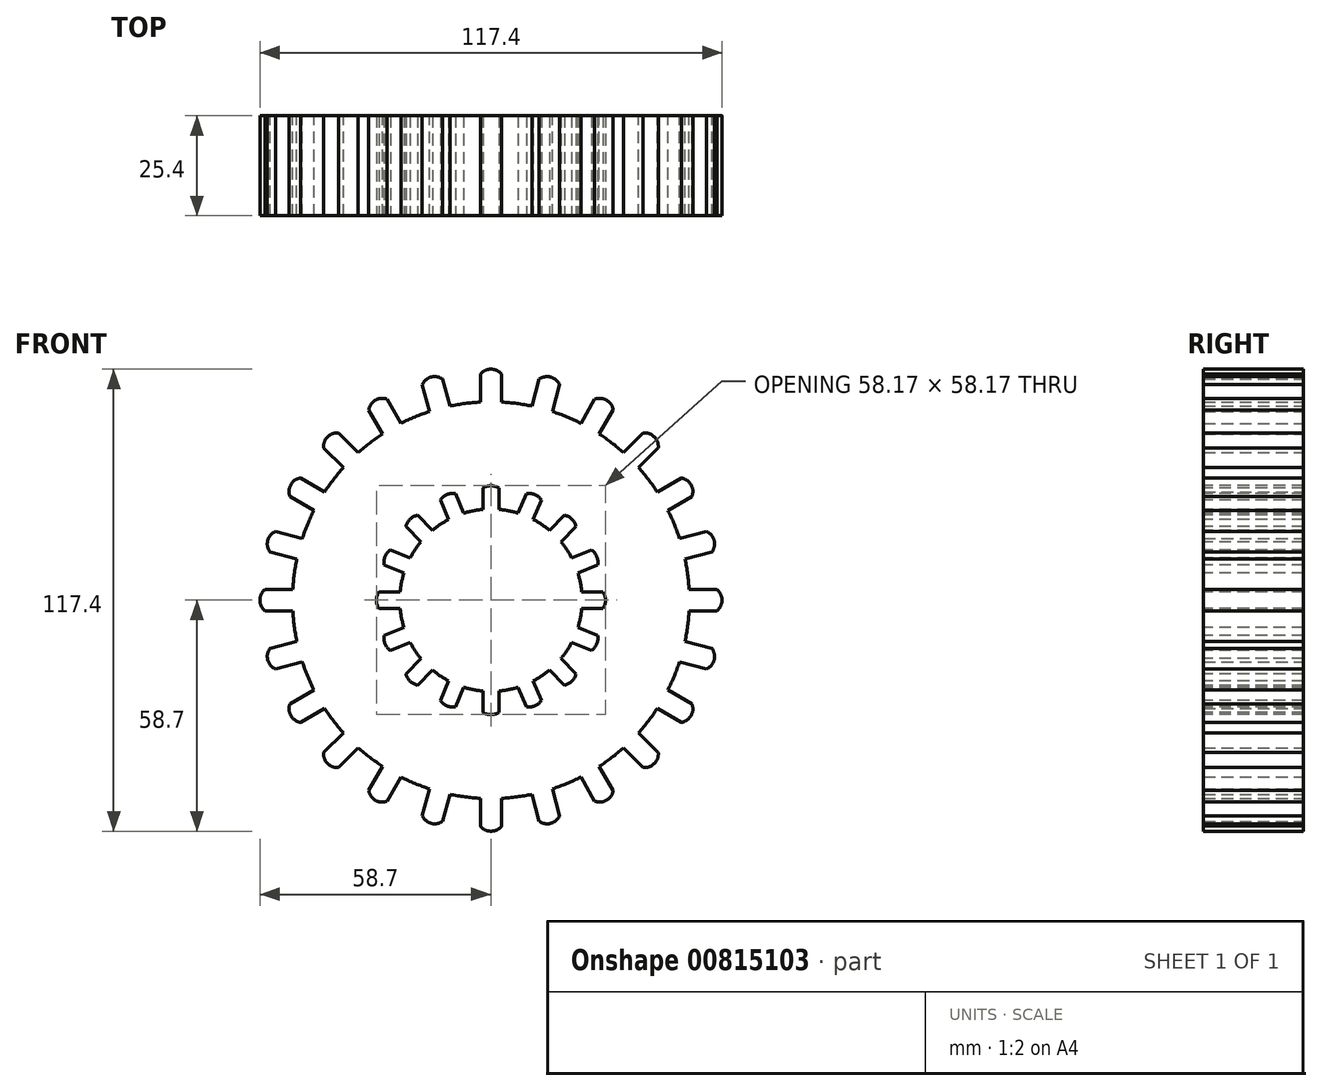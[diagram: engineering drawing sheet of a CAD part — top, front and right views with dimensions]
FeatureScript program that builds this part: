
annotation { "Feature Type Name" : "Feature", "Feature Type Description" : "" }
export const myFeature = defineFeature(function(context is Context, id is Id, definition is map)
    precondition{}
    {
        {
            var Q0;
            Q0=qCreatedBy(makeId("Front.planeOp"),FACE);
            var sketch = newSketch(context, id + "F0", { "sketchPlane" : qUnion([Q0])});
            skCircle(sketch, "E0", {"center": v(0, 0) * mm, "radius": 50.41 * mm});
            skLineSegment(sketch, "E1", {"start": v(2.7, 57.4) * mm, "end": v(2.7, 50.34) * mm});
            skLineSegment(sketch, "E2.MirrorCS", {"start": v(-2.7, 57.4) * mm, "end": v(-2.7, 50.34) * mm});
            skArc(sketch, "E3", {"start": v(2.7, 57.4) * mm, "mid": v(0, 58.7) * mm, "end": v(-2.7, 57.4) * mm});
            skLineSegment(sketch, "E4.1.0", {"start": v(-17.46, 54.75) * mm, "end": v(-15.63, 47.93) * mm});
            skArc(sketch, "E4.1.1", {"start": v(-12.25, 56.15) * mm, "mid": v(-15.2, 56.7) * mm, "end": v(-17.46, 54.75) * mm});
            skLineSegment(sketch, "E4.1.2", {"start": v(-12.25, 56.15) * mm, "end": v(-10.43, 49.32) * mm});
            skLineSegment(sketch, "E4.2.0", {"start": v(-31.04, 48.37) * mm, "end": v(-27.5, 42.25) * mm});
            skArc(sketch, "E4.2.1", {"start": v(-26.37, 51.06) * mm, "mid": v(-29.35, 50.84) * mm, "end": v(-31.04, 48.37) * mm});
            skLineSegment(sketch, "E4.2.2", {"start": v(-26.37, 51.06) * mm, "end": v(-22.84, 44.94) * mm});
            skLineSegment(sketch, "E4.3.0", {"start": v(-42.5, 38.69) * mm, "end": v(-37.5, 33.7) * mm});
            skArc(sketch, "E4.3.1", {"start": v(-38.69, 42.5) * mm, "mid": v(-41.5, 41.5) * mm, "end": v(-42.5, 38.69) * mm});
            skLineSegment(sketch, "E4.3.2", {"start": v(-38.69, 42.5) * mm, "end": v(-33.7, 37.5) * mm});
            skLineSegment(sketch, "E4.4.0", {"start": v(-51.06, 26.37) * mm, "end": v(-44.94, 22.84) * mm});
            skArc(sketch, "E4.4.1", {"start": v(-48.37, 31.04) * mm, "mid": v(-50.84, 29.35) * mm, "end": v(-51.06, 26.37) * mm});
            skLineSegment(sketch, "E4.4.2", {"start": v(-48.37, 31.04) * mm, "end": v(-42.25, 27.5) * mm});
            skLineSegment(sketch, "E4.5.0", {"start": v(-56.15, 12.25) * mm, "end": v(-49.32, 10.43) * mm});
            skArc(sketch, "E4.5.1", {"start": v(-54.75, 17.46) * mm, "mid": v(-56.7, 15.2) * mm, "end": v(-56.15, 12.25) * mm});
            skLineSegment(sketch, "E4.5.2", {"start": v(-54.75, 17.46) * mm, "end": v(-47.93, 15.63) * mm});
            skLineSegment(sketch, "E4.6.0", {"start": v(-57.4, -2.7) * mm, "end": v(-50.34, -2.7) * mm});
            skArc(sketch, "E4.6.1", {"start": v(-57.4, 2.7) * mm, "mid": v(-58.7, 0) * mm, "end": v(-57.4, -2.7) * mm});
            skLineSegment(sketch, "E4.6.2", {"start": v(-57.4, 2.7) * mm, "end": v(-50.34, 2.7) * mm});
            skLineSegment(sketch, "E4.7.0", {"start": v(-54.75, -17.46) * mm, "end": v(-47.93, -15.63) * mm});
            skArc(sketch, "E4.7.1", {"start": v(-56.15, -12.25) * mm, "mid": v(-56.7, -15.2) * mm, "end": v(-54.75, -17.46) * mm});
            skLineSegment(sketch, "E4.7.2", {"start": v(-56.15, -12.25) * mm, "end": v(-49.32, -10.43) * mm});
            skLineSegment(sketch, "E4.8.0", {"start": v(-48.37, -31.04) * mm, "end": v(-42.25, -27.5) * mm});
            skArc(sketch, "E4.8.1", {"start": v(-51.06, -26.37) * mm, "mid": v(-50.84, -29.35) * mm, "end": v(-48.37, -31.04) * mm});
            skLineSegment(sketch, "E4.8.2", {"start": v(-51.06, -26.37) * mm, "end": v(-44.94, -22.84) * mm});
            skLineSegment(sketch, "E4.9.0", {"start": v(-38.69, -42.5) * mm, "end": v(-33.7, -37.5) * mm});
            skArc(sketch, "E4.9.1", {"start": v(-42.5, -38.69) * mm, "mid": v(-41.5, -41.5) * mm, "end": v(-38.69, -42.5) * mm});
            skLineSegment(sketch, "E4.9.2", {"start": v(-42.5, -38.69) * mm, "end": v(-37.5, -33.7) * mm});
            skLineSegment(sketch, "E4.10.0", {"start": v(-26.37, -51.06) * mm, "end": v(-22.84, -44.94) * mm});
            skArc(sketch, "E4.10.1", {"start": v(-31.04, -48.37) * mm, "mid": v(-29.35, -50.84) * mm, "end": v(-26.37, -51.06) * mm});
            skLineSegment(sketch, "E4.10.2", {"start": v(-31.04, -48.37) * mm, "end": v(-27.5, -42.25) * mm});
            skLineSegment(sketch, "E4.11.0", {"start": v(-12.25, -56.15) * mm, "end": v(-10.43, -49.32) * mm});
            skArc(sketch, "E4.11.1", {"start": v(-17.46, -54.75) * mm, "mid": v(-15.2, -56.7) * mm, "end": v(-12.25, -56.15) * mm});
            skLineSegment(sketch, "E4.11.2", {"start": v(-17.46, -54.75) * mm, "end": v(-15.63, -47.93) * mm});
            skLineSegment(sketch, "E4.12.0", {"start": v(2.7, -57.4) * mm, "end": v(2.7, -50.34) * mm});
            skArc(sketch, "E4.12.1", {"start": v(-2.7, -57.4) * mm, "mid": v(0, -58.7) * mm, "end": v(2.7, -57.4) * mm});
            skLineSegment(sketch, "E4.12.2", {"start": v(-2.7, -57.4) * mm, "end": v(-2.7, -50.34) * mm});
            skLineSegment(sketch, "E4.13.0", {"start": v(17.46, -54.75) * mm, "end": v(15.63, -47.93) * mm});
            skArc(sketch, "E4.13.1", {"start": v(12.25, -56.15) * mm, "mid": v(15.2, -56.7) * mm, "end": v(17.46, -54.75) * mm});
            skLineSegment(sketch, "E4.13.2", {"start": v(12.25, -56.15) * mm, "end": v(10.43, -49.32) * mm});
            skLineSegment(sketch, "E4.14.0", {"start": v(31.04, -48.37) * mm, "end": v(27.5, -42.25) * mm});
            skArc(sketch, "E4.14.1", {"start": v(26.37, -51.06) * mm, "mid": v(29.35, -50.84) * mm, "end": v(31.04, -48.37) * mm});
            skLineSegment(sketch, "E4.14.2", {"start": v(26.37, -51.06) * mm, "end": v(22.84, -44.94) * mm});
            skLineSegment(sketch, "E4.15.0", {"start": v(42.5, -38.69) * mm, "end": v(37.5, -33.7) * mm});
            skArc(sketch, "E4.15.1", {"start": v(38.69, -42.5) * mm, "mid": v(41.5, -41.5) * mm, "end": v(42.5, -38.69) * mm});
            skLineSegment(sketch, "E4.15.2", {"start": v(38.69, -42.5) * mm, "end": v(33.7, -37.5) * mm});
            skLineSegment(sketch, "E4.16.0", {"start": v(51.06, -26.37) * mm, "end": v(44.94, -22.84) * mm});
            skArc(sketch, "E4.16.1", {"start": v(48.37, -31.04) * mm, "mid": v(50.84, -29.35) * mm, "end": v(51.06, -26.37) * mm});
            skLineSegment(sketch, "E4.16.2", {"start": v(48.37, -31.04) * mm, "end": v(42.25, -27.5) * mm});
            skLineSegment(sketch, "E4.17.0", {"start": v(56.15, -12.25) * mm, "end": v(49.32, -10.43) * mm});
            skArc(sketch, "E4.17.1", {"start": v(54.75, -17.46) * mm, "mid": v(56.7, -15.2) * mm, "end": v(56.15, -12.25) * mm});
            skLineSegment(sketch, "E4.17.2", {"start": v(54.75, -17.46) * mm, "end": v(47.93, -15.63) * mm});
            skLineSegment(sketch, "E4.18.0", {"start": v(57.4, 2.7) * mm, "end": v(50.34, 2.7) * mm});
            skArc(sketch, "E4.18.1", {"start": v(57.4, -2.7) * mm, "mid": v(58.7, 0) * mm, "end": v(57.4, 2.7) * mm});
            skLineSegment(sketch, "E4.18.2", {"start": v(57.4, -2.7) * mm, "end": v(50.34, -2.7) * mm});
            skLineSegment(sketch, "E4.19.0", {"start": v(54.75, 17.46) * mm, "end": v(47.93, 15.63) * mm});
            skArc(sketch, "E4.19.1", {"start": v(56.15, 12.25) * mm, "mid": v(56.7, 15.2) * mm, "end": v(54.75, 17.46) * mm});
            skLineSegment(sketch, "E4.19.2", {"start": v(56.15, 12.25) * mm, "end": v(49.32, 10.43) * mm});
            skLineSegment(sketch, "E4.20.0", {"start": v(48.37, 31.04) * mm, "end": v(42.25, 27.5) * mm});
            skArc(sketch, "E4.20.1", {"start": v(51.06, 26.37) * mm, "mid": v(50.84, 29.35) * mm, "end": v(48.37, 31.04) * mm});
            skLineSegment(sketch, "E4.20.2", {"start": v(51.06, 26.37) * mm, "end": v(44.94, 22.84) * mm});
            skLineSegment(sketch, "E4.21.0", {"start": v(38.69, 42.5) * mm, "end": v(33.7, 37.5) * mm});
            skArc(sketch, "E4.21.1", {"start": v(42.5, 38.69) * mm, "mid": v(41.5, 41.5) * mm, "end": v(38.69, 42.5) * mm});
            skLineSegment(sketch, "E4.21.2", {"start": v(42.5, 38.69) * mm, "end": v(37.5, 33.7) * mm});
            skLineSegment(sketch, "E4.22.0", {"start": v(26.37, 51.06) * mm, "end": v(22.84, 44.94) * mm});
            skArc(sketch, "E4.22.1", {"start": v(31.04, 48.37) * mm, "mid": v(29.35, 50.84) * mm, "end": v(26.37, 51.06) * mm});
            skLineSegment(sketch, "E4.22.2", {"start": v(31.04, 48.37) * mm, "end": v(27.5, 42.25) * mm});
            skLineSegment(sketch, "E4.23.0", {"start": v(12.25, 56.15) * mm, "end": v(10.43, 49.32) * mm});
            skArc(sketch, "E4.23.1", {"start": v(17.46, 54.75) * mm, "mid": v(15.2, 56.7) * mm, "end": v(12.25, 56.15) * mm});
            skLineSegment(sketch, "E4.23.2", {"start": v(17.46, 54.75) * mm, "end": v(15.63, 47.93) * mm});
            skSolve(sketch);
        }
        {
            var Q0;
            Q0=qCreatedBy(makeId("Front.planeOp"),FACE);
            var sketch = newSketch(context, id + "F1", { "sketchPlane" : qUnion([Q0])});
            skCircle(sketch, "E5", {"center": v(0, 0) * mm, "radius": 23.16 * mm});
            skLineSegment(sketch, "E6", {"start": v(2.07, 28.48) * mm, "end": v(2.07, 23.07) * mm});
            skLineSegment(sketch, "E7.MirrorCS", {"start": v(-2.07, 28.48) * mm, "end": v(-2.07, 23.07) * mm});
            skArc(sketch, "E8", {"start": v(2.07, 28.48) * mm, "mid": v(0, 29.09) * mm, "end": v(-2.07, 28.48) * mm});
            skLineSegment(sketch, "E9.1.0", {"start": v(-12.81, 25.52) * mm, "end": v(-10.74, 20.52) * mm});
            skArc(sketch, "E9.1.1", {"start": v(-8.99, 27.1) * mm, "mid": v(-11.13, 26.87) * mm, "end": v(-12.81, 25.52) * mm});
            skLineSegment(sketch, "E9.1.2", {"start": v(-8.99, 27.1) * mm, "end": v(-6.92, 22.1) * mm});
            skLineSegment(sketch, "E9.2.0", {"start": v(-21.6, 18.67) * mm, "end": v(-17.77, 14.85) * mm});
            skArc(sketch, "E9.2.1", {"start": v(-18.67, 21.6) * mm, "mid": v(-20.57, 20.57) * mm, "end": v(-21.6, 18.67) * mm});
            skLineSegment(sketch, "E9.2.2", {"start": v(-18.67, 21.6) * mm, "end": v(-14.85, 17.77) * mm});
            skLineSegment(sketch, "E9.3.0", {"start": v(-27.1, 8.99) * mm, "end": v(-22.1, 6.92) * mm});
            skArc(sketch, "E9.3.1", {"start": v(-25.52, 12.81) * mm, "mid": v(-26.87, 11.13) * mm, "end": v(-27.1, 8.99) * mm});
            skLineSegment(sketch, "E9.3.2", {"start": v(-25.52, 12.81) * mm, "end": v(-20.52, 10.74) * mm});
            skLineSegment(sketch, "E9.4.0", {"start": v(-28.48, -2.07) * mm, "end": v(-23.07, -2.07) * mm});
            skArc(sketch, "E9.4.1", {"start": v(-28.48, 2.07) * mm, "mid": v(-29.09, 0) * mm, "end": v(-28.48, -2.07) * mm});
            skLineSegment(sketch, "E9.4.2", {"start": v(-28.48, 2.07) * mm, "end": v(-23.07, 2.07) * mm});
            skLineSegment(sketch, "E9.5.0", {"start": v(-25.52, -12.81) * mm, "end": v(-20.52, -10.74) * mm});
            skArc(sketch, "E9.5.1", {"start": v(-27.1, -8.99) * mm, "mid": v(-26.87, -11.13) * mm, "end": v(-25.52, -12.81) * mm});
            skLineSegment(sketch, "E9.5.2", {"start": v(-27.1, -8.99) * mm, "end": v(-22.1, -6.92) * mm});
            skLineSegment(sketch, "E9.6.0", {"start": v(-18.67, -21.6) * mm, "end": v(-14.85, -17.77) * mm});
            skArc(sketch, "E9.6.1", {"start": v(-21.6, -18.67) * mm, "mid": v(-20.57, -20.57) * mm, "end": v(-18.67, -21.6) * mm});
            skLineSegment(sketch, "E9.6.2", {"start": v(-21.6, -18.67) * mm, "end": v(-17.77, -14.85) * mm});
            skLineSegment(sketch, "E9.7.0", {"start": v(-8.99, -27.1) * mm, "end": v(-6.92, -22.1) * mm});
            skArc(sketch, "E9.7.1", {"start": v(-12.81, -25.52) * mm, "mid": v(-11.13, -26.87) * mm, "end": v(-8.99, -27.1) * mm});
            skLineSegment(sketch, "E9.7.2", {"start": v(-12.81, -25.52) * mm, "end": v(-10.74, -20.52) * mm});
            skLineSegment(sketch, "E9.8.0", {"start": v(2.07, -28.48) * mm, "end": v(2.07, -23.07) * mm});
            skArc(sketch, "E9.8.1", {"start": v(-2.07, -28.48) * mm, "mid": v(0, -29.09) * mm, "end": v(2.07, -28.48) * mm});
            skLineSegment(sketch, "E9.8.2", {"start": v(-2.07, -28.48) * mm, "end": v(-2.07, -23.07) * mm});
            skLineSegment(sketch, "E9.9.0", {"start": v(12.81, -25.52) * mm, "end": v(10.74, -20.52) * mm});
            skArc(sketch, "E9.9.1", {"start": v(8.99, -27.1) * mm, "mid": v(11.13, -26.87) * mm, "end": v(12.81, -25.52) * mm});
            skLineSegment(sketch, "E9.9.2", {"start": v(8.99, -27.1) * mm, "end": v(6.92, -22.1) * mm});
            skLineSegment(sketch, "E9.10.0", {"start": v(21.6, -18.67) * mm, "end": v(17.77, -14.85) * mm});
            skArc(sketch, "E9.10.1", {"start": v(18.67, -21.6) * mm, "mid": v(20.57, -20.57) * mm, "end": v(21.6, -18.67) * mm});
            skLineSegment(sketch, "E9.10.2", {"start": v(18.67, -21.6) * mm, "end": v(14.85, -17.77) * mm});
            skLineSegment(sketch, "E9.11.0", {"start": v(27.1, -8.99) * mm, "end": v(22.1, -6.92) * mm});
            skArc(sketch, "E9.11.1", {"start": v(25.52, -12.81) * mm, "mid": v(26.87, -11.13) * mm, "end": v(27.1, -8.99) * mm});
            skLineSegment(sketch, "E9.11.2", {"start": v(25.52, -12.81) * mm, "end": v(20.52, -10.74) * mm});
            skLineSegment(sketch, "E9.12.0", {"start": v(28.48, 2.07) * mm, "end": v(23.07, 2.07) * mm});
            skArc(sketch, "E9.12.1", {"start": v(28.48, -2.07) * mm, "mid": v(29.09, 0) * mm, "end": v(28.48, 2.07) * mm});
            skLineSegment(sketch, "E9.12.2", {"start": v(28.48, -2.07) * mm, "end": v(23.07, -2.07) * mm});
            skLineSegment(sketch, "E9.13.0", {"start": v(25.52, 12.81) * mm, "end": v(20.52, 10.74) * mm});
            skArc(sketch, "E9.13.1", {"start": v(27.1, 8.99) * mm, "mid": v(26.87, 11.13) * mm, "end": v(25.52, 12.81) * mm});
            skLineSegment(sketch, "E9.13.2", {"start": v(27.1, 8.99) * mm, "end": v(22.1, 6.92) * mm});
            skLineSegment(sketch, "E9.14.0", {"start": v(18.67, 21.6) * mm, "end": v(14.85, 17.77) * mm});
            skArc(sketch, "E9.14.1", {"start": v(21.6, 18.67) * mm, "mid": v(20.57, 20.57) * mm, "end": v(18.67, 21.6) * mm});
            skLineSegment(sketch, "E9.14.2", {"start": v(21.6, 18.67) * mm, "end": v(17.77, 14.85) * mm});
            skLineSegment(sketch, "E9.15.0", {"start": v(8.99, 27.1) * mm, "end": v(6.92, 22.1) * mm});
            skArc(sketch, "E9.15.1", {"start": v(12.81, 25.52) * mm, "mid": v(11.13, 26.87) * mm, "end": v(8.99, 27.1) * mm});
            skLineSegment(sketch, "E9.15.2", {"start": v(12.81, 25.52) * mm, "end": v(10.74, 20.52) * mm});
            skSolve(sketch);
        }
        {
            var Q0;
            {var subQ0=sQuery(id+"F0.wireOp",EDGE,"E0");var subQ33=makeQuery(id+"F0.imprint","INTERSECT",VERTEX,{"derivedFrom":[subQ0,sQuery(id+"F0.wireOp",EDGE,"E4.18.0")]});Q0=makeQuery(id+"F0.imprint","IMPRINT",FACE,{"disambiguationData":[TD([[makeQuery(id+"F0.imprint","IMPRINT",EDGE,{"disambiguationData":[TD([[subQ33,-1.0]])],"derivedFrom":subQ0}),1.0]])]});}
            var Q1;
            {var subQ0=sQuery(id+"F0.wireOp",EDGE,"E4.1.0");Q1=makeQuery(id+"F0.imprint","IMPRINT",FACE,{"disambiguationData":[TD([[makeQuery(id+"F0.imprint","IMPRINT",EDGE,{"derivedFrom":subQ0}),1.0]])]});}
            var Q2;
            {var subQ0=sQuery(id+"F0.wireOp",EDGE,"E1");Q2=makeQuery(id+"F0.imprint","IMPRINT",FACE,{"disambiguationData":[TD([[makeQuery(id+"F0.imprint","IMPRINT",EDGE,{"derivedFrom":subQ0}),-1.0]])]});}
            var Q3;
            {var subQ0=sQuery(id+"F0.wireOp",EDGE,"E4.23.0");Q3=makeQuery(id+"F0.imprint","IMPRINT",FACE,{"disambiguationData":[TD([[makeQuery(id+"F0.imprint","IMPRINT",EDGE,{"derivedFrom":subQ0}),1.0]])]});}
            var Q4;
            {var subQ0=sQuery(id+"F0.wireOp",EDGE,"E4.22.0");Q4=makeQuery(id+"F0.imprint","IMPRINT",FACE,{"disambiguationData":[TD([[makeQuery(id+"F0.imprint","IMPRINT",EDGE,{"derivedFrom":subQ0}),1.0]])]});}
            var Q5;
            {var subQ0=sQuery(id+"F0.wireOp",EDGE,"E4.21.0");Q5=makeQuery(id+"F0.imprint","IMPRINT",FACE,{"disambiguationData":[TD([[makeQuery(id+"F0.imprint","IMPRINT",EDGE,{"derivedFrom":subQ0}),1.0]])]});}
            var Q6;
            {var subQ0=sQuery(id+"F0.wireOp",EDGE,"E4.20.0");Q6=makeQuery(id+"F0.imprint","IMPRINT",FACE,{"disambiguationData":[TD([[makeQuery(id+"F0.imprint","IMPRINT",EDGE,{"derivedFrom":subQ0}),1.0]])]});}
            var Q7;
            {var subQ0=sQuery(id+"F0.wireOp",EDGE,"E4.19.0");Q7=makeQuery(id+"F0.imprint","IMPRINT",FACE,{"disambiguationData":[TD([[makeQuery(id+"F0.imprint","IMPRINT",EDGE,{"derivedFrom":subQ0}),1.0]])]});}
            var Q8;
            {var subQ0=sQuery(id+"F0.wireOp",EDGE,"E4.18.0");Q8=makeQuery(id+"F0.imprint","IMPRINT",FACE,{"disambiguationData":[TD([[makeQuery(id+"F0.imprint","IMPRINT",EDGE,{"derivedFrom":subQ0}),1.0]])]});}
            var Q9;
            {var subQ0=sQuery(id+"F0.wireOp",EDGE,"E4.17.0");Q9=makeQuery(id+"F0.imprint","IMPRINT",FACE,{"disambiguationData":[TD([[makeQuery(id+"F0.imprint","IMPRINT",EDGE,{"derivedFrom":subQ0}),1.0]])]});}
            var Q10;
            {var subQ0=sQuery(id+"F0.wireOp",EDGE,"E4.16.0");Q10=makeQuery(id+"F0.imprint","IMPRINT",FACE,{"disambiguationData":[TD([[makeQuery(id+"F0.imprint","IMPRINT",EDGE,{"derivedFrom":subQ0}),1.0]])]});}
            var Q11;
            {var subQ0=sQuery(id+"F0.wireOp",EDGE,"E4.15.0");Q11=makeQuery(id+"F0.imprint","IMPRINT",FACE,{"disambiguationData":[TD([[makeQuery(id+"F0.imprint","IMPRINT",EDGE,{"derivedFrom":subQ0}),1.0]])]});}
            var Q12;
            {var subQ0=sQuery(id+"F0.wireOp",EDGE,"E4.14.0");Q12=makeQuery(id+"F0.imprint","IMPRINT",FACE,{"disambiguationData":[TD([[makeQuery(id+"F0.imprint","IMPRINT",EDGE,{"derivedFrom":subQ0}),1.0]])]});}
            var Q13;
            {var subQ0=sQuery(id+"F0.wireOp",EDGE,"E4.13.0");Q13=makeQuery(id+"F0.imprint","IMPRINT",FACE,{"disambiguationData":[TD([[makeQuery(id+"F0.imprint","IMPRINT",EDGE,{"derivedFrom":subQ0}),1.0]])]});}
            var Q14;
            {var subQ0=sQuery(id+"F0.wireOp",EDGE,"E4.12.0");Q14=makeQuery(id+"F0.imprint","IMPRINT",FACE,{"disambiguationData":[TD([[makeQuery(id+"F0.imprint","IMPRINT",EDGE,{"derivedFrom":subQ0}),1.0]])]});}
            var Q15;
            {var subQ0=sQuery(id+"F0.wireOp",EDGE,"E4.11.0");Q15=makeQuery(id+"F0.imprint","IMPRINT",FACE,{"disambiguationData":[TD([[makeQuery(id+"F0.imprint","IMPRINT",EDGE,{"derivedFrom":subQ0}),1.0]])]});}
            var Q16;
            {var subQ0=sQuery(id+"F0.wireOp",EDGE,"E4.10.0");Q16=makeQuery(id+"F0.imprint","IMPRINT",FACE,{"disambiguationData":[TD([[makeQuery(id+"F0.imprint","IMPRINT",EDGE,{"derivedFrom":subQ0}),1.0]])]});}
            var Q17;
            {var subQ0=sQuery(id+"F0.wireOp",EDGE,"E4.9.0");Q17=makeQuery(id+"F0.imprint","IMPRINT",FACE,{"disambiguationData":[TD([[makeQuery(id+"F0.imprint","IMPRINT",EDGE,{"derivedFrom":subQ0}),1.0]])]});}
            var Q18;
            {var subQ0=sQuery(id+"F0.wireOp",EDGE,"E4.8.0");Q18=makeQuery(id+"F0.imprint","IMPRINT",FACE,{"disambiguationData":[TD([[makeQuery(id+"F0.imprint","IMPRINT",EDGE,{"derivedFrom":subQ0}),1.0]])]});}
            var Q19;
            {var subQ0=sQuery(id+"F0.wireOp",EDGE,"E4.7.0");Q19=makeQuery(id+"F0.imprint","IMPRINT",FACE,{"disambiguationData":[TD([[makeQuery(id+"F0.imprint","IMPRINT",EDGE,{"derivedFrom":subQ0}),1.0]])]});}
            var Q20;
            {var subQ0=sQuery(id+"F0.wireOp",EDGE,"E4.6.0");Q20=makeQuery(id+"F0.imprint","IMPRINT",FACE,{"disambiguationData":[TD([[makeQuery(id+"F0.imprint","IMPRINT",EDGE,{"derivedFrom":subQ0}),1.0]])]});}
            var Q21;
            {var subQ0=sQuery(id+"F0.wireOp",EDGE,"E4.5.0");Q21=makeQuery(id+"F0.imprint","IMPRINT",FACE,{"disambiguationData":[TD([[makeQuery(id+"F0.imprint","IMPRINT",EDGE,{"derivedFrom":subQ0}),1.0]])]});}
            var Q22;
            {var subQ0=sQuery(id+"F0.wireOp",EDGE,"E4.4.0");Q22=makeQuery(id+"F0.imprint","IMPRINT",FACE,{"disambiguationData":[TD([[makeQuery(id+"F0.imprint","IMPRINT",EDGE,{"derivedFrom":subQ0}),1.0]])]});}
            var Q23;
            {var subQ0=sQuery(id+"F0.wireOp",EDGE,"E4.3.0");Q23=makeQuery(id+"F0.imprint","IMPRINT",FACE,{"disambiguationData":[TD([[makeQuery(id+"F0.imprint","IMPRINT",EDGE,{"derivedFrom":subQ0}),1.0]])]});}
            var Q24;
            {var subQ0=sQuery(id+"F0.wireOp",EDGE,"E4.2.0");Q24=makeQuery(id+"F0.imprint","IMPRINT",FACE,{"disambiguationData":[TD([[makeQuery(id+"F0.imprint","IMPRINT",EDGE,{"derivedFrom":subQ0}),1.0]])]});}
            extrude(context, id + "F2", {"entities" : qUnion([Q0, Q1, Q2, Q3, Q4, Q5, Q6, Q7, Q8, Q9, Q10, Q11, Q12, Q13, Q14, Q15, Q16, Q17, Q18, Q19, Q20, Q21, Q22, Q23, Q24]), "endBound" : BoundingType.SYMMETRIC, "depth" : 25.4 * mm, "offsetDistance" : 25.4 * mm});
        }
        {
            var Q0;
            Q0 = qSketchRegion(id + "F1", true);
            extrude(context, id + "F3", {"entities" : qUnion([Q0]), "operationType" : NewBodyOperationType.REMOVE, "endBound" : BoundingType.SYMMETRIC, "oppositeDirection" : true, "depth" : 25.4 * mm, "offsetDistance" : 25.4 * mm});
        }
    });
